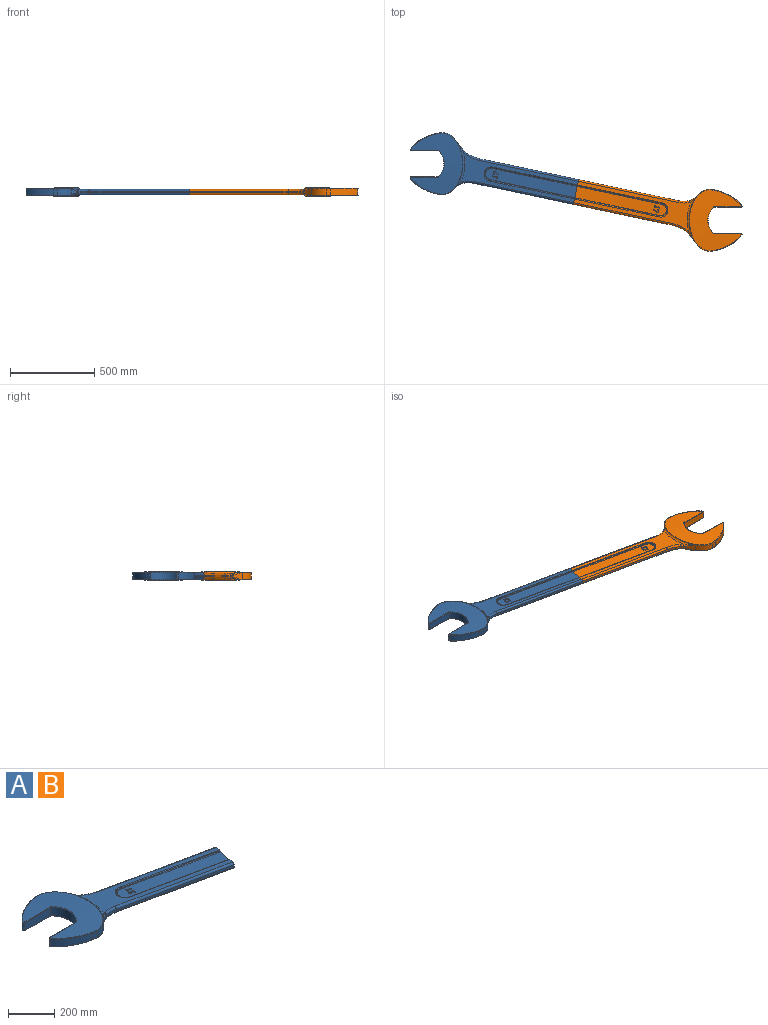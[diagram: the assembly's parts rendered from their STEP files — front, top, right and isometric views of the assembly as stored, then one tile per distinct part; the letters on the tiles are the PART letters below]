
ASSEMBLY  parts=2 mates=1
PART A: 164 faces, bbox 1121.5x429.5x56 mm
  f0: plane 6.07x2.88mm, normal (0,0,1), area 4.6mm2, adj f111,f112,f115,f116,f119,f120,f123,f124
  f1: extruded ~81.82x45.85mm, area 3709.3mm2, adj f7,f12,f138,f140,f156,f158
  f2: extruded ~164.45x94.44mm, area 7435.3mm2, adj f9,f10,f139,f155
  f3: plane 161.63x43.69mm, normal (0,-1,0), area 6798.7mm2, adj f4,f10,f143,f159
  f4: cylinder r=104.25mm len=156.78mm, axis (0,0,-1), area 8058.6mm2, adj f3,f5,f143,f145,f146,f159,f161,f163
  f5: plane 161.63x43.69mm, normal (0,1,0), area 6798.7mm2, adj f4,f11,f146,f163
  f6: extruded ~164.45x94.44mm, area 7435.3mm2, adj f7,f11,f142,f160
  f7: extruded ~36.62x23.95mm, area 882.3mm2, adj f1,f6,f140,f158
  f8: extruded ~87.75x54.13mm, area 4135.1mm2, adj f9,f13,f135,f137,f151,f153
  f9: extruded ~36.62x23.95mm, area 882.3mm2, adj f2,f8,f137,f153
  f10: cylinder r=5mm len=40.44mm, axis (0,0,-1), area 458.2mm2, adj f2,f3,f141,f157
  f11: cylinder r=5mm len=40.44mm, axis (0,0,-1), area 458.2mm2, adj f5,f6,f144,f162
  f12: bspline ~55.66x43.65mm, area 975mm2, adj f1,f15,f18,f24,f27,f30,f136,f138
  f13: bspline ~69.53x62.89mm, area 2151.8mm2, adj f8,f16,f19,f26,f33,f36,f37,f133
  f14: bspline ~267.25x52.08mm, area 2970mm2, adj f15,f16,f21,f132
  f15: bspline ~35.99x28.6mm, area 368mm2, adj f12,f14,f27,f134
  f16: bspline ~57.3x42.41mm, area 557.3mm2, adj f13,f14,f33,f131
  f17: bspline ~267.25x52.08mm, area 2970.6mm2, adj f18,f22,f36,f150
  f18: bspline ~35.33x28.33mm, area 371.6mm2, adj f12,f17,f30,f152
  f19: bspline ~10.06x7mm, area 6.2mm2, adj f13,f36,f147,f148
  f20: plane 146.76x31.03mm, normal (0.98,-0.21,0), area 3794.4mm2, adj f21,f22,f23,f25,f29,f32,f34,f38
  f21: plane 698.64x298.72mm, normal (0,0,-1), area 42595.6mm2, adj f14,f20,f27,f28,f29,f33,f34,f35
  f22: plane 698.65x298.72mm, normal (0,0,1), area 42595.2mm2, adj f17,f20,f30,f31,f32,f37,f38,f39
  f23: plane 586.6x124.01mm, normal (0.21,0.98,0), area 6595.2mm2, adj f20,f26,f34,f38
  f24: cylinder r=127.23mm len=59.66mm, axis (0,0,-1), area 662.7mm2, adj f12,f25,f28,f31
  f25: plane 597.38x126.29mm, normal (-0.21,-0.98,0), area 6716.4mm2, adj f20,f24,f29,f32
  f26: cylinder r=207.12mm len=76.53mm, axis (0,0,-1), area 922.5mm2, adj f13,f23,f35,f39
  f27: bspline ~42.63x21.43mm, area 158.2mm2, adj f12,f15,f21,f28
  f28: torus R=137.23mm, axis (0,0,1), area 973.4mm2, adj f21,f24,f27,f29
  f29: cylinder r=10mm len=599.45mm, axis (0.98,-0.21,0), area 9591mm2, adj f20,f21,f25,f28
  f30: bspline ~42.65x21.49mm, area 158.2mm2, adj f12,f18,f22,f31
  f31: torus R=137.23mm, axis (0,0,-1), area 973.4mm2, adj f22,f24,f30,f32
  f32: cylinder r=10mm len=599.45mm, axis (0.98,-0.21,0), area 9591mm2, adj f20,f22,f25,f31
  f33: bspline ~53.94x46.5mm, area 315.3mm2, adj f13,f16,f21,f35
  f34: cylinder r=10mm len=588.66mm, axis (-0.98,0.21,0), area 9417.7mm2, adj f20,f21,f23,f35
  f35: torus R=217.12mm, axis (0,0,1), area 1340.3mm2, adj f21,f26,f33,f34
  f36: bspline ~55.78x41.31mm, area 555.5mm2, adj f13,f17,f19,f37,f148
  f37: bspline ~53.94x46.5mm, area 315.3mm2, adj f13,f22,f36,f39
  f38: cylinder r=10mm len=588.66mm, axis (-0.98,0.21,0), area 9417.7mm2, adj f20,f22,f23,f39
  f39: torus R=217.12mm, axis (0,0,-1), area 1340.3mm2, adj f22,f26,f37,f38
  f40: plane 545.25x174.14mm, normal (0,0,1), area 36752.9mm2, adj f20,f41,f42,f43,f56,f57,f58,f59
  f41: cylinder r=5mm len=504.92mm, axis (0.98,-0.21,0), area 2697.4mm2, adj f20,f40,f42,f44
  f42: torus R=34.16mm, axis (0,0,1), area 601.2mm2, adj f40,f41,f43,f45
  f43: cylinder r=5mm len=504.92mm, axis (-0.98,0.21,0), area 2697.4mm2, adj f20,f40,f42,f46
  f44: cylinder r=5mm len=504.92mm, axis (0.98,-0.21,0), area 2697.4mm2, adj f20,f22,f41,f45
  f45: torus R=42.82mm, axis (0,0,-1), area 665.1mm2, adj f22,f42,f44,f46
  f46: cylinder r=5mm len=504.92mm, axis (-0.98,0.21,0), area 2697.4mm2, adj f20,f22,f43,f45
  f47: plane 545.25x174.14mm, normal (0,0,-1), area 37029.2mm2, adj f20,f48,f49,f50
  f48: cylinder r=5mm len=504.92mm, axis (-0.98,0.21,0), area 2697.4mm2, adj f20,f47,f49,f51
  f49: torus R=34.16mm, axis (0,0,-1), area 601.2mm2, adj f47,f48,f50,f52
  f50: cylinder r=5mm len=504.92mm, axis (0.98,-0.21,0), area 2697.4mm2, adj f20,f47,f49,f53
  f51: cylinder r=5mm len=504.92mm, axis (-0.98,0.21,0), area 2697.4mm2, adj f20,f21,f48,f52
  f52: torus R=42.82mm, axis (0,0,1), area 665.1mm2, adj f21,f49,f51,f53
  f53: cylinder r=5mm len=504.92mm, axis (0.98,-0.21,0), area 2697.4mm2, adj f20,f21,f50,f52
  f54: bspline ~372x369.06mm, area 60560.6mm2, adj f147,f148,f149,f150,f151,f152,f153,f154
  f55: bspline ~372x369.06mm, area 60560.1mm2, adj f131,f132,f133,f134,f135,f136,f137,f138
  f56: plane 2.2x1.6mm, normal (-0.21,-0.98,0), area 3.6mm2, adj f40,f57,f82,f106
  f57: plane 14.49x3.06mm, normal (0.98,-0.21,0), area 32.6mm2, adj f40,f56,f58,f104
  f58: plane 2.2x1.6mm, normal (0.21,0.98,0), area 3.6mm2, adj f40,f57,f59,f105
  f59: plane 2.2x1.86mm, normal (-0.98,0.21,0), area 4.2mm2, adj f40,f58,f60,f107
  f60: extruded ~2.2x1.2mm, area 2.8mm2, adj f40,f59,f61,f109
  f61: extruded ~2.2x0.91mm, area 2.4mm2, adj f40,f60,f62,f113
  f62: extruded ~2.2x0.97mm, area 2.4mm2, adj f40,f61,f63,f117
  f63: extruded ~2.2x1.48mm, area 3.3mm2, adj f40,f62,f64,f121
  f64: plane 22.98x4.86mm, normal (0.21,0.98,0), area 51.7mm2, adj f40,f63,f65,f125
  f65: plane 2.44x2.2mm, normal (-0.98,0.21,0), area 5.5mm2, adj f40,f64,f66,f129
  f66: plane 3.09x2.2mm, normal (-0.91,-0.41,0), area 7.5mm2, adj f40,f65,f67,f130
  f67: extruded ~2.2x1.97mm, area 4.7mm2, adj f40,f66,f68,f128
  f68: extruded ~2.2x1.61mm, area 3.7mm2, adj f40,f67,f69,f124
  f69: extruded ~2.2x1.36mm, area 3.1mm2, adj f40,f68,f70,f120
  f70: extruded ~2.2x1.24mm, area 2.7mm2, adj f40,f69,f71,f116
  f71: extruded ~2.2x1.59mm, area 3.6mm2, adj f40,f70,f72,f112
  f72: extruded ~2.2x1.26mm, area 3.4mm2, adj f40,f71,f73,f111
  f73: extruded ~2.2x1.18mm, area 2.6mm2, adj f40,f72,f74,f115
  f74: extruded ~2.2x1.33mm, area 3.2mm2, adj f40,f73,f75,f119
  f75: extruded ~2.2x1.51mm, area 4mm2, adj f40,f74,f76,f123
  f76: extruded ~2.2x1.72mm, area 4.8mm2, adj f40,f75,f77,f127
  f77: plane 19.99x4.23mm, normal (-0.21,-0.98,0), area 45mm2, adj f40,f76,f78,f126
  f78: extruded ~2.2x1.38mm, area 3.3mm2, adj f40,f77,f79,f122
  f79: extruded ~2.2x0.84mm, area 2.4mm2, adj f40,f78,f80,f118
  f80: extruded ~2.2x1.06mm, area 2.4mm2, adj f40,f79,f81,f114
  f81: extruded ~2.2x1.24mm, area 2.7mm2, adj f40,f80,f82,f110
  f82: plane 2.54x2.2mm, normal (-0.98,0.21,0), area 5.7mm2, adj f40,f56,f81,f108
  f83: plane 27.09x13.39mm, normal (0,0,1), area 66mm2, adj f104,f105,f106,f107,f108,f109,f110,f113
  f84: plane 22.18x14.06mm, normal (-0.54,-0.84,0), area 57.8mm2, adj f40,f85,f93,f99
  f85: plane 2.86x2.2mm, normal (0.98,-0.21,0), area 6.4mm2, adj f40,f84,f86,f97
  f86: plane 24.05x14.87mm, normal (0.53,0.85,0), area 62.2mm2, adj f40,f85,f87,f95
  f87: plane 3.19x1.48mm, normal (0.21,0.98,0), area 3mm2, adj f40,f86,f88,f95,f96
  f88: plane 17.02x3.6mm, normal (-0.98,0.21,0), area 38.3mm2, adj f40,f87,f89,f96
  f89: plane 6.84x2.2mm, normal (-0.23,-0.97,0), area 15.5mm2, adj f40,f88,f90,f98
  f90: plane 2.2x1.6mm, normal (0.98,-0.21,0), area 3.6mm2, adj f40,f89,f91,f100
  f91: plane 2.2x1.87mm, normal (0.28,0.96,0), area 4.3mm2, adj f40,f90,f92,f102
  f92: extruded ~2.62x2.2mm, area 7.4mm2, adj f40,f91,f93,f103
  f93: plane 9.99x2.2mm, normal (0.98,-0.21,0), area 22.5mm2, adj f40,f84,f92,f101
  f94: plane 26.9x16.81mm, normal (0,0,1), area 51.6mm2, adj f95,f96,f97,f98,f99,f100,f101,f102
  f95: cylinder r=0.8mm len=25.14mm, axis (0.85,-0.53,0), area 35.7mm2, adj f86,f87,f94,f96,f97
  f96: cylinder r=0.8mm len=17.19mm, axis (0.21,0.98,0), area 21.2mm2, adj f87,f88,f94,f95,f98
  f97: cylinder r=0.8mm len=3.03mm, axis (-0.21,-0.98,0), area 2.6mm2, adj f85,f94,f95,f99
  f98: cylinder r=0.8mm len=7.03mm, axis (-0.97,0.23,0), area 7.8mm2, adj f89,f94,f96,f100
  f99: cylinder r=0.8mm len=23.58mm, axis (-0.84,0.54,0), area 33mm2, adj f84,f94,f97,f101
  f100: cylinder r=0.8mm len=1.76mm, axis (-0.21,-0.98,0), area 1.3mm2, adj f90,f94,f98,f102
  f101: cylinder r=0.8mm len=11.29mm, axis (-0.21,-0.98,0), area 13.6mm2, adj f93,f94,f99,f103
  f102: cylinder r=0.8mm len=2.09mm, axis (0.96,-0.28,0), area 2mm2, adj f91,f94,f100,f103
  f103: bspline ~4.34x2.55mm, area 4.8mm2, adj f92,f94,f101,f102
  f104: cylinder r=0.8mm len=14.65mm, axis (-0.21,-0.98,0), area 17.6mm2, adj f57,f83,f105,f106
  f105: cylinder r=0.8mm len=1.76mm, axis (0.98,-0.21,0), area 1.3mm2, adj f58,f83,f104,f107
  f106: cylinder r=0.8mm len=1.76mm, axis (-0.98,0.21,0), area 1.3mm2, adj f56,f83,f104,f108
  f107: cylinder r=0.8mm len=2.02mm, axis (0.21,0.98,0), area 1.9mm2, adj f59,f83,f105,f109
  f108: cylinder r=0.8mm len=2.71mm, axis (0.21,0.98,0), area 2.8mm2, adj f82,f83,f106,f110
  f109: bspline ~1.96x1.27mm, area 1.6mm2, adj f60,f83,f107,f113
  f110: bspline ~1.88x1.03mm, area 1.6mm2, adj f81,f83,f108,f114
  f111: bspline ~2.05x1.72mm, area 1.7mm2, adj f0,f72,f112,f115
  f112: bspline ~2.4x1.23mm, area 1.4mm2, adj f0,f71,f111,f116
  f113: bspline ~1.72x1.54mm, area 1.5mm2, adj f61,f83,f109,f117
  f114: bspline ~1.91x1.08mm, area 1.5mm2, adj f80,f83,f110,f118
  f115: bspline ~1.73x0.94mm, area 1.3mm2, adj f0,f73,f111,f119
  f116: bspline ~1.89x0.97mm, area 1.2mm2, adj f0,f70,f112,f120
  f117: bspline ~1.85x1.38mm, area 1.6mm2, adj f62,f83,f113,f121
  f118: bspline ~1.78x1.58mm, area 1.6mm2, adj f79,f83,f114,f122
  f119: bspline ~1.9x1.38mm, area 1.7mm2, adj f0,f74,f115,f123
  f120: bspline ~2.11x1.2mm, area 1.8mm2, adj f0,f69,f116,f124
  f121: bspline ~2.54x0.99mm, area 2mm2, adj f63,f83,f117,f125
  f122: bspline ~2.52x1.64mm, area 2mm2, adj f78,f83,f118,f126
  f123: bspline ~2.28x1.85mm, area 2.2mm2, adj f0,f75,f119,f127
  f124: bspline ~2.51x1.51mm, area 2.2mm2, adj f0,f68,f120,f128
  f125: cylinder r=0.8mm len=23.15mm, axis (0.98,-0.21,0), area 29mm2, adj f64,f83,f121,f129
  f126: cylinder r=0.8mm len=21.81mm, axis (-0.98,0.21,0), area 26.6mm2, adj f77,f83,f122,f127,f130
  f127: bspline ~4.65x3.91mm, area 3.8mm2, adj f0,f76,f123,f126,f130
  f128: bspline ~2.77x1.75mm, area 2.7mm2, adj f0,f67,f124,f130
  f129: cylinder r=0.8mm len=2.6mm, axis (0.21,0.98,0), area 2.5mm2, adj f65,f83,f125,f130
  f130: cylinder r=0.8mm len=3.42mm, axis (-0.41,0.91,0), area 3.9mm2, adj f0,f66,f83,f126,f127,f128,f129
  f131: bspline ~11.44x8.04mm, area 24.2mm2, adj f16,f55,f132,f133
  f132: bspline ~261.58x42.67mm, area 653mm2, adj f14,f55,f131,f134
  f133: bspline ~29.48x22.46mm, area 34.6mm2, adj f13,f55,f131,f135
  f134: bspline ~9.11x8.19mm, area 19.1mm2, adj f15,f55,f132,f136
  f135: bspline ~100.81x61.72mm, area 326.3mm2, adj f8,f13,f55,f133,f137
  f136: bspline ~8.39x6.84mm, area 6.8mm2, adj f12,f55,f134,f138
  f137: bspline ~35.2x6.94mm, area 73.3mm2, adj f8,f9,f55,f135,f139
  f138: bspline ~92.57x50.26mm, area 295.1mm2, adj f1,f12,f55,f136,f140
  f139: bspline ~175.78x100.45mm, area 595.1mm2, adj f2,f55,f137,f141
  f140: bspline ~35.2x6.94mm, area 73.3mm2, adj f1,f7,f55,f138,f142
  f141: bspline ~8.44x5.29mm, area 30.4mm2, adj f10,f55,f139,f143
  f142: bspline ~200.57x104.98mm, area 595.1mm2, adj f6,f55,f140,f144
  f143: bspline ~308.33x5.15mm, area 514.3mm2, adj f3,f4,f55,f141,f145
  f144: bspline ~9x6.12mm, area 30.4mm2, adj f11,f55,f142,f146
  f145: bspline ~173.71x46.77mm, area 562.5mm2, adj f4,f55,f143,f146
  f146: bspline ~308.33x5.15mm, area 514.3mm2, adj f4,f5,f55,f144,f145
  f147: bspline ~10.14x7.83mm, area 18.8mm2, adj f19,f54,f148,f149
  f148: bspline ~8.93x5.86mm, area 13mm2, adj f19,f36,f54,f147,f150
  f149: bspline ~29.53x22.4mm, area 26.4mm2, adj f13,f54,f147,f151
  f150: bspline ~265.54x45.06mm, area 653.4mm2, adj f17,f54,f148,f152
  f151: bspline ~99.81x60.49mm, area 326.3mm2, adj f8,f13,f54,f149,f153
  f152: bspline ~7.82x7.39mm, area 19mm2, adj f18,f54,f150,f154
  f153: bspline ~35.2x6.94mm, area 73.3mm2, adj f8,f9,f54,f151,f155
  f154: bspline ~8.91x7.11mm, area 6.3mm2, adj f12,f54,f152,f156
  f155: bspline ~200.57x104.98mm, area 595.1mm2, adj f2,f54,f153,f157
  f156: bspline ~94.05x51.55mm, area 295.1mm2, adj f1,f12,f54,f154,f158
  f157: bspline ~9x6.12mm, area 30.4mm2, adj f10,f54,f155,f159
  f158: bspline ~35.2x6.94mm, area 73.3mm2, adj f1,f7,f54,f156,f160
  f159: bspline ~308.33x5.15mm, area 514.3mm2, adj f3,f4,f54,f157,f161
  f160: bspline ~175.78x100.45mm, area 595.1mm2, adj f6,f54,f158,f162
  f161: bspline ~173.71x46.77mm, area 562.5mm2, adj f4,f54,f159,f163
  f162: bspline ~9x5.29mm, area 30.4mm2, adj f11,f54,f160,f163
  f163: bspline ~308.33x5.15mm, area 514.3mm2, adj f4,f5,f54,f161,f162
PART B: same geometry as A
PLACE A at identity
PLACE B rot(axis=(0,0,1),180deg) t=(1595.4,-337.27,0)mm
MATE fastened B.f20 <-> A.f20  axis (-0.98,0.21,0) through (797.7,-168.64,27.5)mm
